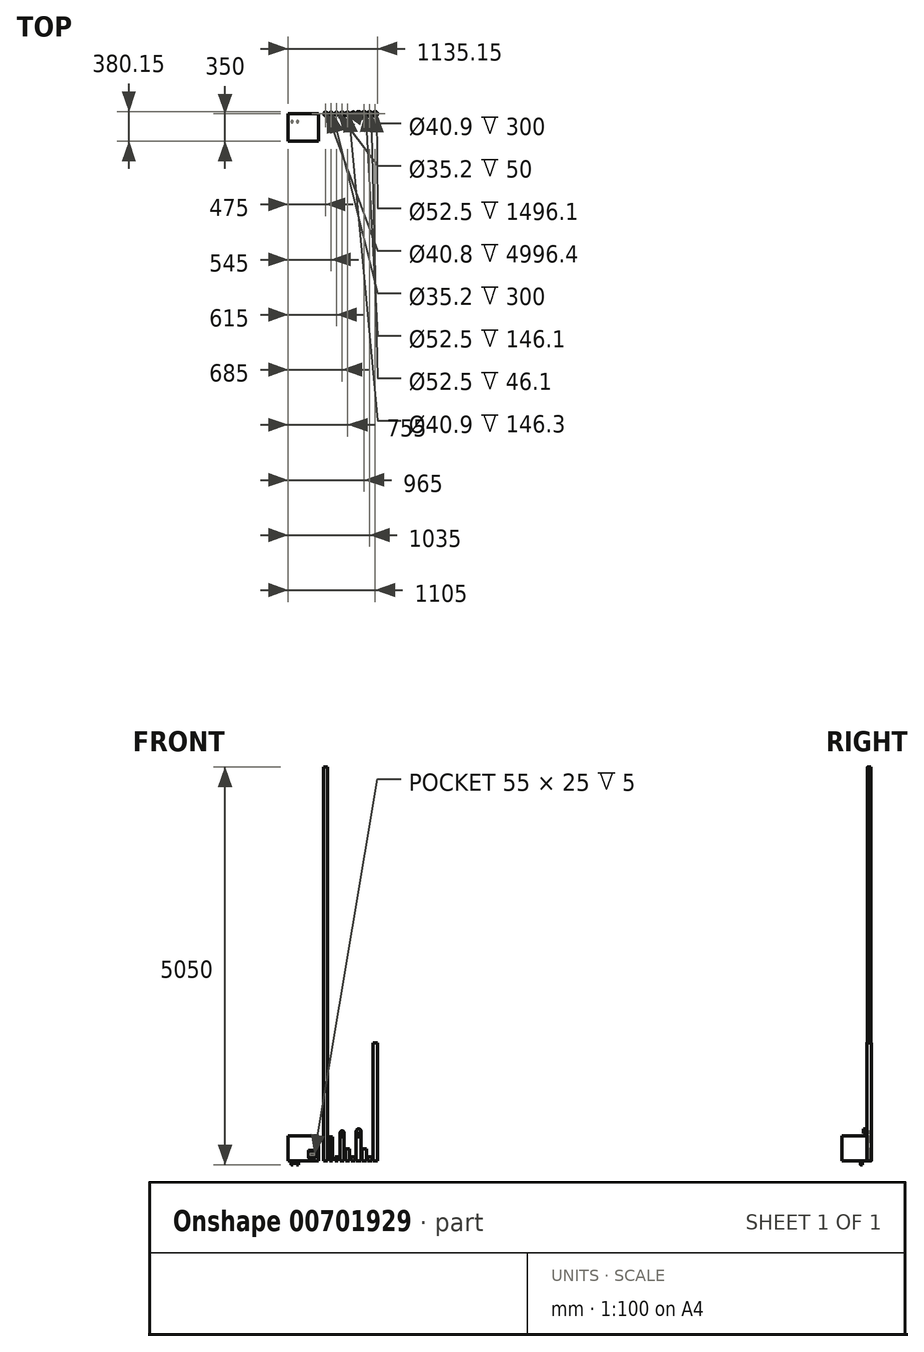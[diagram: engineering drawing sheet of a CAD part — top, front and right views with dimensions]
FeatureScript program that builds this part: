
annotation { "Feature Type Name" : "Feature", "Feature Type Description" : "" }
export const myFeature = defineFeature(function(context is Context, id is Id, definition is map)
    precondition{}
    {
        {
            var Q0;
            Q0=qCreatedBy(makeId("Top.planeOp"),FACE);
            var sketch = newSketch(context, id + "F0", { "sketchPlane" : qUnion([Q0])});
            skCircle(sketch, "E0", {"center": v(0, 0) * mm, "radius": 21.2 * mm});
            skCircle(sketch, "E1", {"center": v(-70, 0) * mm, "radius": 24 * mm});
            skSolve(sketch);
        }
        {
            var Q0;
            Q0=makeQuery(id+"F0.imprint","IMPRINT",FACE,{"disambiguationData":[TD([[makeQuery(id+"F0.imprint","IMPRINT",EDGE,{"derivedFrom":sQuery(id+"F0.wireOp",EDGE,"E0")}),1.0]])]});
            extrude(context, id + "F1", {"entities" : qUnion([Q0]), "depth" : 300 * mm, "offsetDistance" : 25 * mm});
        }
        {
            var Q0;
            Q0=qCreatedBy(makeId("Top.planeOp"),FACE);
            var sketch = newSketch(context, id + "F2", { "sketchPlane" : qUnion([Q0])});
            skCircle(sketch, "E2", {"center": v(70, 0) * mm, "radius": 21.2 * mm});
            skSolve(sketch);
        }
        {
            var Q0;
            Q0=makeQuery(id+"F2.imprint","IMPRINT",FACE,{"disambiguationData":[TD([[makeQuery(id+"F2.imprint","IMPRINT",EDGE,{"derivedFrom":sQuery(id+"F2.wireOp",EDGE,"E2")}),1.0]])]});
            extrude(context, id + "F3", {"entities" : qUnion([Q0]), "depth" : 50 * mm, "offsetDistance" : 25 * mm});
        }
        {
            var Q0;
            Q0=qCreatedBy(makeId("Top.planeOp"),FACE);
            var sketch = newSketch(context, id + "F4", { "sketchPlane" : qUnion([Q0])});
            skCircle(sketch, "E3", {"center": v(140, 0) * mm, "radius": 24.15 * mm});
            skCircle(sketch, "E4", {"center": v(210, 0) * mm, "radius": 24.15 * mm});
            skCircle(sketch, "E5", {"center": v(280, 0) * mm, "radius": 24.15 * mm});
            skCircle(sketch, "E6", {"center": v(350, 0) * mm, "radius": 30.15 * mm});
            skCircle(sketch, "E7", {"center": v(420, 0) * mm, "radius": 30.15 * mm});
            skCircle(sketch, "E8", {"center": v(490, 0) * mm, "radius": 30.15 * mm});
            skCircle(sketch, "E9", {"center": v(560, 0) * mm, "radius": 30.15 * mm});
            skSolve(sketch);
        }
        {
            var Q0;
            Q0=makeQuery(id+"F4.imprint","IMPRINT",FACE,{"disambiguationData":[TD([[makeQuery(id+"F4.imprint","IMPRINT",EDGE,{"derivedFrom":sQuery(id+"F4.wireOp",EDGE,"E3")}),1.0]])]});
            extrude(context, id + "F5", {"entities" : qUnion([Q0]), "depth" : 300 * mm, "offsetDistance" : 25 * mm});
        }
        {
            var Q0;
            Q0=makeQuery(id+"F1.opExtrude","CAP_FACE",FACE,{"disambiguationData":[OSD([sQuery(id+"F0.wireOp",EDGE,"E0")])],"isStart":false});
            var Q1;
            Q1=makeQuery(id+"F1.opExtrude","CAP_FACE",FACE,{"disambiguationData":[OSD([sQuery(id+"F0.wireOp",EDGE,"E0")])],"isStart":true});
            shell(context, id + "F6", {"entities" : qUnion([Q0, Q1]), "thickness" : 3.6 * mm});
        }
        {
            var Q0;
            Q0=makeQuery(id+"F3.opExtrude","CAP_FACE",FACE,{"disambiguationData":[OSD([sQuery(id+"F2.wireOp",EDGE,"E2")])],"isStart":false});
            var Q1;
            Q1=makeQuery(id+"F3.opExtrude","CAP_FACE",FACE,{"disambiguationData":[OSD([sQuery(id+"F2.wireOp",EDGE,"E2")])],"isStart":true});
            shell(context, id + "F7", {"entities" : qUnion([Q0, Q1]), "thickness" : 3.6 * mm});
        }
        {
            var Q0;
            Q0=makeQuery(id+"F5.opExtrude","CAP_FACE",FACE,{"disambiguationData":[OSD([sQuery(id+"F4.wireOp",EDGE,"E3")])],"isStart":true});
            var Q1;
            Q1=makeQuery(id+"F5.opExtrude","CAP_FACE",FACE,{"disambiguationData":[OSD([sQuery(id+"F4.wireOp",EDGE,"E3")])],"isStart":false});
            shell(context, id + "F8", {"entities" : qUnion([Q0, Q1]), "thickness" : 3.7 * mm});
        }
        {
            var Q0;
            Q0=makeQuery(id+"F4.imprint","IMPRINT",FACE,{"disambiguationData":[TD([[makeQuery(id+"F4.imprint","IMPRINT",EDGE,{"derivedFrom":sQuery(id+"F4.wireOp",EDGE,"E4")}),1.0]])]});
            extrude(context, id + "F9", {"entities" : qUnion([Q0]), "depth" : 150 * mm, "offsetDistance" : 25 * mm});
        }
        {
            var Q0;
            Q0=makeQuery(id+"F4.imprint","IMPRINT",FACE,{"disambiguationData":[TD([[makeQuery(id+"F4.imprint","IMPRINT",EDGE,{"derivedFrom":sQuery(id+"F4.wireOp",EDGE,"E5")}),1.0]])]});
            extrude(context, id + "F10", {"entities" : qUnion([Q0]), "depth" : 50 * mm, "offsetDistance" : 25 * mm});
        }
        {
            var Q0;
            Q0=makeQuery(id+"F4.imprint","IMPRINT",FACE,{"disambiguationData":[TD([[makeQuery(id+"F4.imprint","IMPRINT",EDGE,{"derivedFrom":sQuery(id+"F4.wireOp",EDGE,"E6")}),1.0]])]});
            extrude(context, id + "F11", {"entities" : qUnion([Q0]), "depth" : 300 * mm, "offsetDistance" : 25 * mm});
        }
        {
            var Q0;
            Q0=makeQuery(id+"F4.imprint","IMPRINT",FACE,{"disambiguationData":[TD([[makeQuery(id+"F4.imprint","IMPRINT",EDGE,{"derivedFrom":sQuery(id+"F4.wireOp",EDGE,"E7")}),1.0]])]});
            extrude(context, id + "F12", {"entities" : qUnion([Q0]), "depth" : 150 * mm, "offsetDistance" : 25 * mm});
        }
        {
            var Q0;
            Q0=makeQuery(id+"F4.imprint","IMPRINT",FACE,{"disambiguationData":[TD([[makeQuery(id+"F4.imprint","IMPRINT",EDGE,{"derivedFrom":sQuery(id+"F4.wireOp",EDGE,"E8")}),1.0]])]});
            extrude(context, id + "F13", {"entities" : qUnion([Q0]), "depth" : 50 * mm, "offsetDistance" : 25 * mm});
        }
        {
            var Q0;
            Q0=makeQuery(id+"F9.opExtrude","CAP_FACE",FACE,{"disambiguationData":[OSD([sQuery(id+"F4.wireOp",EDGE,"E4")])],"isStart":false});
            shell(context, id + "F14", {"entities" : qUnion([Q0]), "thickness" : 3.7 * mm});
        }
        {
            var Q0;
            Q0=qCreatedBy(makeId("Right.planeOp"),FACE);
            cPlane(context, id + "F15", {"entities" : qUnion([Q0]), "cplaneType" : CPlaneType.OFFSET, "offset" : 140 * mm, "width" : 150 * mm, "height" : 150 * mm});
        }
        {
            var Q0;
            Q0=qCreatedBy(id+"F15.planeOp",FACE);
            cPlane(context, id + "F16", {"entities" : qUnion([Q0]), "cplaneType" : CPlaneType.OFFSET, "offset" : 210 * mm, "width" : 150 * mm, "height" : 150 * mm});
        }
        {
            var Q0;
            Q0=qCreatedBy(id+"F15.planeOp",FACE);
            var sketch = newSketch(context, id + "F17", { "sketchPlane" : qUnion([Q0])});
            skLineSegment(sketch, "E10", {"start": v(0, 300) * mm, "end": v(0, 300) * mm});
            skLineSegment(sketch, "E11", {"start": v(-57, 357) * mm, "end": v(-57, 357) * mm});
            skPoint(sketch, "E12.visualSharp", {"position": v(0, 357) * mm});
            skArc(sketch, "E12.filletArc", {"start": v(0, 300) * mm, "mid": v(-16.7, 340.3) * mm, "end": v(-57, 357) * mm});
            skSolve(sketch);
        }
        {
            var Q0;
            Q0=makeQuery(id+"F5.opExtrude","CAP_FACE",FACE,{"disambiguationData":[OSD([sQuery(id+"F4.wireOp",EDGE,"E3")])],"isStart":false});
            var sketch = newSketch(context, id + "F18", { "sketchPlane" : qUnion([Q0])});
            skCircle(sketch, "E13.0", {"center": v(140, 0) * mm, "radius": 24.15 * mm});
            skSolve(sketch);
        }
        {
            var Q0;
            Q0=makeQuery(id+"F18.imprint","IMPRINT",FACE,{"disambiguationData":[TD([[makeQuery(id+"F18.imprint","IMPRINT",EDGE,{"derivedFrom":sQuery(id+"F18.wireOp",EDGE,"E13.0")}),1.0]])]});
            var Q1;
            Q1=sQuery(id+"F17.wireOp",EDGE,"E10");
            var Q2;
            Q2=sQuery(id+"F17.wireOp",EDGE,"E12.filletArc");
            var Q3;
            Q3=sQuery(id+"F17.wireOp",EDGE,"E11");
            sweep(context, id + "F19", {"profiles" : qUnion([Q0]), "path" : qUnion([Q1, Q2, Q3])});
        }
        {
            var Q0;
            Q0=qCreatedBy(id+"F16.planeOp",FACE);
            var sketch = newSketch(context, id + "F20", { "sketchPlane" : qUnion([Q0])});
            skLineSegment(sketch, "E14", {"start": v(0, 300) * mm, "end": v(0, 300.68) * mm});
            skLineSegment(sketch, "E15", {"start": v(-76, 376) * mm, "end": v(-76, 376) * mm});
            skPoint(sketch, "E16.visualSharp", {"position": v(0, 376) * mm});
            skArc(sketch, "E16.filletArc", {"start": v(0, 300) * mm, "mid": v(-22.26, 353.74) * mm, "end": v(-76, 376) * mm});
            skSolve(sketch);
        }
        {
            var Q0;
            Q0=makeQuery(id+"F11.opExtrude","CAP_FACE",FACE,{"disambiguationData":[OSD([sQuery(id+"F4.wireOp",EDGE,"E6")])],"isStart":false});
            var Q1;
            Q1=sQuery(id+"F20.wireOp",EDGE,"E16.filletArc");
            sweep(context, id + "F21", {"profiles" : qUnion([Q0]), "path" : qUnion([Q1])});
        }
        {
            var Q0;
            Q0=makeQuery(id+"F21.opSweep","CAP_FACE",FACE,{"disambiguationData":[OSD([sQuery(id+"F4.wireOp",EDGE,"E6"),sQuery(id+"F20.wireOp",VERTEX,"E16.filletArc.end")])],"isStart":false});
            shell(context, id + "F22", {"entities" : qUnion([Q0]), "thickness" : 3.9 * mm});
        }
        {
            var Q0;
            Q0=makeQuery(id+"F12.opExtrude","CAP_FACE",FACE,{"disambiguationData":[OSD([sQuery(id+"F4.wireOp",EDGE,"E7")])],"isStart":false});
            shell(context, id + "F23", {"entities" : qUnion([Q0]), "thickness" : 3.9 * mm});
        }
        {
            var Q0;
            Q0=makeQuery(id+"F13.opExtrude","CAP_FACE",FACE,{"disambiguationData":[OSD([sQuery(id+"F4.wireOp",EDGE,"E8")])],"isStart":false});
            shell(context, id + "F24", {"entities" : qUnion([Q0]), "thickness" : 3.9 * mm});
        }
        {
            var Q0;
            Q0=makeQuery(id+"F0.imprint","IMPRINT",FACE,{"disambiguationData":[TD([[makeQuery(id+"F0.imprint","IMPRINT",EDGE,{"derivedFrom":sQuery(id+"F0.wireOp",EDGE,"E1")}),1.0]])]});
            extrude(context, id + "F25", {"entities" : qUnion([Q0]), "depth" : 5000 * mm, "offsetDistance" : 25 * mm});
        }
        {
            var Q0;
            Q0=makeQuery(id+"F25.opExtrude","CAP_FACE",FACE,{"disambiguationData":[OSD([sQuery(id+"F0.wireOp",EDGE,"E1")])],"isStart":false});
            shell(context, id + "F26", {"entities" : qUnion([Q0]), "thickness" : 3.6 * mm});
        }
        {
            var Q0;
            Q0=makeQuery(id+"F4.imprint","IMPRINT",FACE,{"disambiguationData":[TD([[makeQuery(id+"F4.imprint","IMPRINT",EDGE,{"derivedFrom":sQuery(id+"F4.wireOp",EDGE,"E9")}),1.0]])]});
            extrude(context, id + "F27", {"entities" : qUnion([Q0]), "depth" : 1500 * mm, "offsetDistance" : 25 * mm});
        }
        {
            var Q0;
            Q0=makeQuery(id+"F27.opExtrude","CAP_FACE",FACE,{"disambiguationData":[OSD([sQuery(id+"F4.wireOp",EDGE,"E9")])],"isStart":false});
            shell(context, id + "F28", {"entities" : qUnion([Q0]), "thickness" : 3.9 * mm});
        }
        {
            var Q0;
            Q0=qCreatedBy(makeId("Front.planeOp"),FACE);
            var sketch = newSketch(context, id + "F29", { "sketchPlane" : qUnion([Q0])});
            skLineSegment(sketch, "E17.bottom", {"start": v(-160, 0) * mm, "end": v(-545, 0) * mm});
            skLineSegment(sketch, "E17.top", {"start": v(-160, 315) * mm, "end": v(-545, 315) * mm});
            skLineSegment(sketch, "E17.left", {"start": v(-160, 0) * mm, "end": v(-160, 315) * mm});
            skLineSegment(sketch, "E17.right", {"start": v(-545, 0) * mm, "end": v(-545, 315) * mm});
            skSolve(sketch);
        }
        {
            var Q0;
            Q0=makeQuery(id+"F29.imprint","IMPRINT",FACE,{"disambiguationData":[TD([[makeQuery(id+"F29.imprint","IMPRINT",EDGE,{"derivedFrom":sQuery(id+"F29.wireOp",EDGE,"E17.bottom")}),-1.0]])]});
            extrude(context, id + "F30", {"entities" : qUnion([Q0]), "depth" : 345 * mm, "offsetDistance" : 25 * mm});
        }
        {
            var Q0;
            Q0=makeQuery(id+"F30.opExtrude","CAP_FACE",FACE,{"disambiguationData":[OSD([sQuery(id+"F29.wireOp",EDGE,"E17.bottom"),sQuery(id+"F29.wireOp",EDGE,"E17.top"),sQuery(id+"F29.wireOp",EDGE,"E17.left"),sQuery(id+"F29.wireOp",EDGE,"E17.right")])],"isStart":false});
            var sketch = newSketch(context, id + "F31", { "sketchPlane" : qUnion([Q0])});
            skLineSegment(sketch, "E18.bottom", {"start": v(-289.5, 134.12) * mm, "end": v(-194.5, 134.12) * mm});
            skLineSegment(sketch, "E18.top", {"start": v(-289.5, 34.12) * mm, "end": v(-194.5, 34.12) * mm});
            skLineSegment(sketch, "E18.left", {"start": v(-289.5, 134.12) * mm, "end": v(-289.5, 34.12) * mm});
            skLineSegment(sketch, "E18.right", {"start": v(-194.5, 134.12) * mm, "end": v(-194.5, 34.12) * mm});
            skSolve(sketch);
        }
        {
            var Q0;
            Q0=makeQuery(id+"F31.imprint","IMPRINT",FACE,{"disambiguationData":[TD([[makeQuery(id+"F31.imprint","IMPRINT",EDGE,{"derivedFrom":sQuery(id+"F31.wireOp",EDGE,"E18.bottom")}),-1.0]])]});
            extrude(context, id + "F32", {"entities" : qUnion([Q0]), "operationType" : NewBodyOperationType.ADD, "depth" : 5 * mm, "offsetDistance" : 25 * mm});
        }
        {
            var Q0;
            Q0=makeQuery(id+"F32.opExtrude","SWEPT_EDGE",EDGE,{"disambiguationData":[OSD([sQuery(id+"F31.wireOp",EDGE,"E18.bottom"),sQuery(id+"F31.wireOp",EDGE,"E18.left")])]});
            var Q1;
            Q1=makeQuery(id+"F32.opExtrude","SWEPT_EDGE",EDGE,{"disambiguationData":[OSD([sQuery(id+"F31.wireOp",EDGE,"E18.bottom"),sQuery(id+"F31.wireOp",EDGE,"E18.right")])]});
            var Q2;
            Q2=makeQuery(id+"F32.opExtrude","SWEPT_EDGE",EDGE,{"disambiguationData":[OSD([sQuery(id+"F31.wireOp",EDGE,"E18.top"),sQuery(id+"F31.wireOp",EDGE,"E18.right")])]});
            var Q3;
            Q3=makeQuery(id+"F32.opExtrude","SWEPT_EDGE",EDGE,{"disambiguationData":[OSD([sQuery(id+"F31.wireOp",EDGE,"E18.top"),sQuery(id+"F31.wireOp",EDGE,"E18.left")])]});
            fillet(context, id + "F33", {"entities" : qUnion([Q0, Q1, Q2, Q3]), "radius" : 10 * mm, "tangentPropagation" : true, "allowEdgeOverflow" : false});
        }
        {
            var Q0;
            Q0=makeQuery(id+"F32.opExtrude","CAP_FACE",FACE,{"disambiguationData":[OSD([sQuery(id+"F31.wireOp",EDGE,"E18.bottom"),sQuery(id+"F31.wireOp",EDGE,"E18.top"),sQuery(id+"F31.wireOp",EDGE,"E18.left"),sQuery(id+"F31.wireOp",EDGE,"E18.right")])],"isStart":false});
            var sketch = newSketch(context, id + "F34", { "sketchPlane" : qUnion([Q0])});
            skLineSegment(sketch, "E19.bottom", {"start": v(-266.4, 91.4) * mm, "end": v(-211.4, 91.4) * mm});
            skLineSegment(sketch, "E19.top", {"start": v(-266.4, 66.4) * mm, "end": v(-211.4, 66.4) * mm});
            skLineSegment(sketch, "E19.left", {"start": v(-266.4, 91.4) * mm, "end": v(-266.4, 66.4) * mm});
            skLineSegment(sketch, "E19.right", {"start": v(-211.4, 91.4) * mm, "end": v(-211.4, 66.4) * mm});
            skSolve(sketch);
        }
        {
            var Q0;
            Q0=makeQuery(id+"F34.imprint","IMPRINT",FACE,{"disambiguationData":[TD([[makeQuery(id+"F34.imprint","IMPRINT",EDGE,{"derivedFrom":sQuery(id+"F34.wireOp",EDGE,"E19.bottom")}),-1.0]])]});
            extrude(context, id + "F35", {"entities" : qUnion([Q0]), "operationType" : NewBodyOperationType.REMOVE, "oppositeDirection" : true, "depth" : 5 * mm, "offsetDistance" : 25 * mm});
        }
        {
            var Q0;
            Q0=makeQuery(id+"F30.opExtrude","SWEPT_FACE",FACE,{"disambiguationData":[OSD([sQuery(id+"F29.wireOp",EDGE,"E17.bottom")])]});
            var sketch = newSketch(context, id + "F36", { "sketchPlane" : qUnion([Q0])});
            skCircle(sketch, "E20", {"center": v(-425, 100) * mm, "radius": 12.5 * mm});
            skCircle(sketch, "E21", {"center": v(-495, 100) * mm, "radius": 12.5 * mm});
            skSolve(sketch);
        }
        {
            var Q0;
            Q0=makeQuery(id+"F36.imprint","IMPRINT",FACE,{"disambiguationData":[TD([[makeQuery(id+"F36.imprint","IMPRINT",EDGE,{"derivedFrom":sQuery(id+"F36.wireOp",EDGE,"E21")}),1.0]])]});
            var Q1;
            Q1=makeQuery(id+"F36.imprint","IMPRINT",FACE,{"disambiguationData":[TD([[makeQuery(id+"F36.imprint","IMPRINT",EDGE,{"derivedFrom":sQuery(id+"F36.wireOp",EDGE,"E20")}),1.0]])]});
            extrude(context, id + "F37", {"entities" : qUnion([Q0, Q1]), "operationType" : NewBodyOperationType.ADD, "depth" : 50 * mm, "offsetDistance" : 25 * mm});
        }
    });
